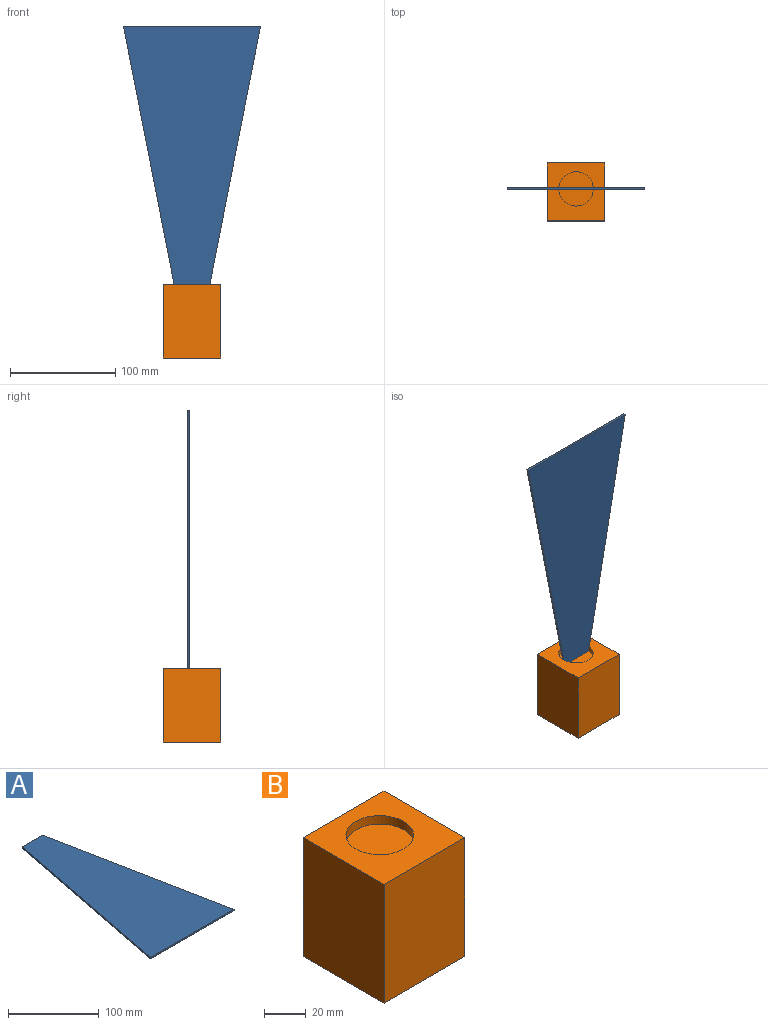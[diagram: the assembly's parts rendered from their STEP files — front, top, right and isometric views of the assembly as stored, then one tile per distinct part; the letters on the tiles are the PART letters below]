
ASSEMBLY  parts=2 mates=1
PART A: 6 faces, bbox 130x250x2 mm
  f0: plane 130x2mm, normal (0,-1,0), area 260mm2, adj f1,f3,f4,f5
  f1: plane 250x49mm, normal (0.98,0.19,0), area 509.5mm2, adj f0,f2,f4,f5
  f2: plane 32x2mm, normal (0,1,0), area 64mm2, adj f1,f3,f4,f5
  f3: plane 250x49mm, normal (-0.98,0.19,0), area 509.5mm2, adj f0,f2,f4,f5
  f4: plane 250x130mm, normal (0,0,1), area 20250mm2, adj f0,f1,f2,f3
  f5: plane 250x130mm, normal (0,0,-1), area 20250mm2, adj f0,f1,f2,f3
PART B: 8 faces, bbox 55x55x70 mm
  f0: plane 70x55mm, normal (-1,0,0), area 3850mm2, adj f1,f3,f4,f5
  f1: plane 70x55mm, normal (0,-1,0), area 3850mm2, adj f0,f2,f4,f5
  f2: plane 70x55mm, normal (1,0,0), area 3850mm2, adj f1,f3,f4,f5
  f3: plane 70x55mm, normal (0,1,0), area 3850mm2, adj f0,f2,f4,f5
  f4: plane 55x55mm, normal (0,0,1), area 2191.7mm2, adj f0,f1,f2,f3,f6
  f5: plane 55x55mm, normal (0,0,-1), area 3025mm2, adj f0,f1,f2,f3
  f6: cylinder r=16.29mm len=32.57mm, axis (0,0,1), area 511.6mm2, adj f4,f7
  f7: plane 32.57x32.57mm, normal (0,0,1), area 833.3mm2, adj f6
PLACE A rot(axis=(-1,0,0),90deg) t=(79.29,29.43,180.88)mm
PLACE B t=(-20.74,0.03,2.02)mm fixed
MATE planar A.f2 <-> B.f6  axis (0,0,-1) through (6.76,30.43,67.02)mm
